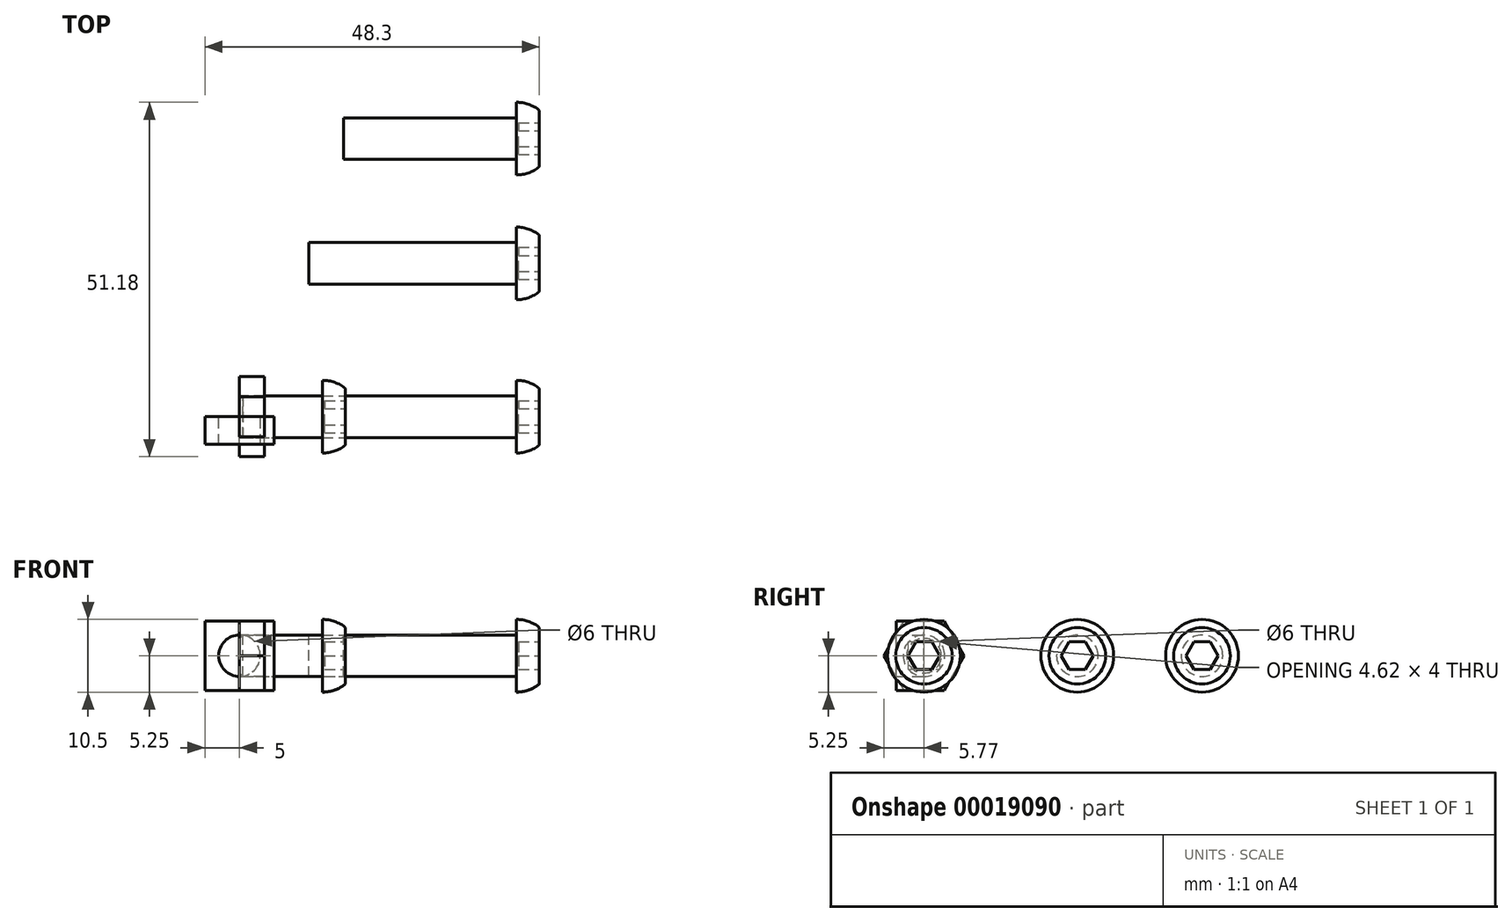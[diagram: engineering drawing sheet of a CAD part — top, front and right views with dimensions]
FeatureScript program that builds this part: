
annotation { "Feature Type Name" : "Feature", "Feature Type Description" : "" }
export const myFeature = defineFeature(function(context is Context, id is Id, definition is map)
    precondition{}
    {
        {
            var Q0;
            Q0=qCreatedBy(makeId("Right.planeOp"),FACE);
            var sketch = newSketch(context, id + "F0", { "sketchPlane" : qUnion([Q0])});
            skCircle(sketch, "E0.cCircle", {"center": v(0, 0) * mm, "radius": 5 * mm, "construction": true});
            skLineSegment(sketch, "E0.0", {"start": v(5.77, 0) * mm, "end": v(2.89, -5) * mm});
            skLineSegment(sketch, "E0.1", {"start": v(2.89, -5) * mm, "end": v(-2.89, -5) * mm});
            skLineSegment(sketch, "E0.2", {"start": v(-2.89, -5) * mm, "end": v(-5.77, 0) * mm});
            skLineSegment(sketch, "E0.3", {"start": v(-5.77, 0) * mm, "end": v(-2.89, 5) * mm});
            skLineSegment(sketch, "E0.4", {"start": v(-2.89, 5) * mm, "end": v(2.89, 5) * mm});
            skLineSegment(sketch, "E0.5", {"start": v(2.89, 5) * mm, "end": v(5.77, 0) * mm});
            skPoint(sketch, "E0.0.midPoint", {"position": v(4.33, -2.5) * mm});
            skLineSegment(sketch, "E1", {"start": v(0, 0) * mm, "end": v(17.46, 0) * mm, "construction": true});
            skCircle(sketch, "E2", {"center": v(0, 0) * mm, "radius": 3 * mm});
            skSolve(sketch);
        }
        {
            var Q0;
            Q0=qCreatedBy(makeId("Top.planeOp"),FACE);
            var sketch = newSketch(context, id + "F1", { "sketchPlane" : qUnion([Q0])});
            skLineSegment(sketch, "E3.top", {"start": v(40, 3) * mm, "end": v(0, 3) * mm});
            skLineSegment(sketch, "E3.bottom", {"start": v(40, 0) * mm, "end": v(0, 0) * mm});
            skLineSegment(sketch, "E3.right", {"start": v(0, 0) * mm, "end": v(0, 3) * mm});
            skPoint(sketch, "E4", {"position": v(41.65, 0) * mm});
            skLineSegment(sketch, "E5.rect.bottom", {"start": v(40, 5.25) * mm, "end": v(43.3, 5.25) * mm, "construction": true});
            skLineSegment(sketch, "E5.rect.top", {"start": v(40, -5.25) * mm, "end": v(43.3, -5.25) * mm, "construction": true});
            skLineSegment(sketch, "E5.rect.left", {"start": v(40, 5.25) * mm, "end": v(40, -5.25) * mm});
            skLineSegment(sketch, "E5.rect.right", {"start": v(43.3, 5.25) * mm, "end": v(43.3, -5.25) * mm});
            skArc(sketch, "E6", {"start": v(43.3, 4.08) * mm, "mid": v(41.75, 4.95) * mm, "end": v(40, 5.25) * mm});
            skArc(sketch, "E7.MirrorCS", {"start": v(43.3, -4.08) * mm, "mid": v(41.75, -4.95) * mm, "end": v(40, -5.25) * mm});
            skLineSegment(sketch, "E8", {"start": v(40, 0) * mm, "end": v(43.3, 0) * mm});
            skLineSegment(sketch, "E9.MirrorCS", {"start": v(0, 0) * mm, "end": v(0, -3) * mm});
            skLineSegment(sketch, "E10.MirrorCS", {"start": v(40, -3) * mm, "end": v(0, -3) * mm});
            skSolve(sketch);
        }
        {
            var Q0;
            Q0=qSketchRegion(id+"F0",true);
            extrude(context, id + "F2", {"entities" : qUnion([Q0]), "depth" : 3.6 * mm});
        }
        {
            var Q0;
            {var subQ2=sQuery(id+"F1.wireOp",EDGE,"E3.top");Q0=makeQuery(id+"F1.imprint","IMPRINT",FACE,{"disambiguationData":[TD([[makeQuery(id+"F1.imprint","IMPRINT",EDGE,{"derivedFrom":subQ2}),1.0]])]});}
            var Q1;
            {var subQ0=sQuery(id+"F1.wireOp",EDGE,"E6");Q1=makeQuery(id+"F1.imprint","IMPRINT",FACE,{"disambiguationData":[TD([[makeQuery(id+"F1.imprint","IMPRINT",EDGE,{"derivedFrom":subQ0}),1.0]])]});}
            var Q2;
            Q2=sQuery(id+"F1.wireOp",EDGE,"E3.bottom");
            revolve(context, id + "F3", {"entities" : qUnion([Q0, Q1]), "axis" : qUnion([Q2]), "revolveType" : RevolveType.FULL});
        }
        {
            var Q0;
            Q0=makeQuery(id+"F3.opRevolve","SWEPT_FACE",FACE,{"disambiguationData":[OSD([sQuery(id+"F1.wireOp",EDGE,"E5.rect.right")])]});
            cPlane(context, id + "F4", {"entities" : qUnion([Q0]), "cplaneType" : CPlaneType.OFFSET, "offset" : 0 * mm, "width" : 150 * mm, "height" : 150 * mm});
        }
        {
            var Q0;
            Q0=qCreatedBy(id+"F4.planeOp",FACE);
            var sketch = newSketch(context, id + "F5", { "sketchPlane" : qUnion([Q0])});
            skCircle(sketch, "E11.cCircle", {"center": v(0, 0) * mm, "radius": 2 * mm, "construction": true});
            skLineSegment(sketch, "E11.0", {"start": v(2.3, 0) * mm, "end": v(1.15, -2) * mm});
            skLineSegment(sketch, "E11.1", {"start": v(1.15, -2) * mm, "end": v(-1.15, -2) * mm});
            skLineSegment(sketch, "E11.2", {"start": v(-1.15, -2) * mm, "end": v(-2.3, 0) * mm});
            skLineSegment(sketch, "E11.3", {"start": v(-2.3, 0) * mm, "end": v(-1.15, 2) * mm});
            skLineSegment(sketch, "E11.4", {"start": v(-1.15, 2) * mm, "end": v(1.15, 2) * mm});
            skLineSegment(sketch, "E11.5", {"start": v(1.15, 2) * mm, "end": v(2.3, 0) * mm});
            skPoint(sketch, "E11.0.midPoint", {"position": v(1.73, -1) * mm});
            skLineSegment(sketch, "E12", {"start": v(0, 0) * mm, "end": v(8.66, 0) * mm, "construction": true});
            skLineSegment(sketch, "E13", {"start": v(0, 0) * mm, "end": v(1.73, -1) * mm, "construction": true});
            skSolve(sketch);
        }
        {
            var Q0;
            Q0=qSketchRegion(id+"F5",true);
            extrude(context, id + "F6", {"entities" : qUnion([Q0]), "operationType" : NewBodyOperationType.REMOVE, "oppositeDirection" : true, "depth" : 3 * mm});
        }
        {
            var Q0;
            Q0=makeQuery(id+"F3.opRevolve","SWEPT_BODY",BODY,{"disambiguationData":[OSD([sQuery(id+"F1.wireOp",EDGE,"E3.top"),sQuery(id+"F1.wireOp",EDGE,"E3.bottom"),sQuery(id+"F1.wireOp",EDGE,"E3.right"),sQuery(id+"F1.wireOp",EDGE,"E5.rect.left"),sQuery(id+"F1.wireOp",EDGE,"E5.rect.right"),sQuery(id+"F1.wireOp",EDGE,"E6"),sQuery(id+"F1.wireOp",EDGE,"E8")])]});
            transform(context, id + "F7", {"entities" : qUnion([Q0]), "transformType" : TransformType.TRANSLATION_3D, "dx" : 0 * mm, "dy" : 22.14 * mm, "dz" : 0 * mm, "makeCopy" : true});
        }
        {
            var Q0;
            Q0=qCreatedBy(makeId("Front.planeOp"),FACE);
            var sketch = newSketch(context, id + "F8", { "sketchPlane" : qUnion([Q0])});
            skLineSegment(sketch, "E14.rect.bottom", {"start": v(5, -5) * mm, "end": v(-5, -5) * mm});
            skLineSegment(sketch, "E14.rect.top", {"start": v(5, 5) * mm, "end": v(-5, 5) * mm});
            skLineSegment(sketch, "E14.rect.left", {"start": v(5, -5) * mm, "end": v(5, 5) * mm});
            skLineSegment(sketch, "E14.rect.right", {"start": v(-5, -5) * mm, "end": v(-5, 5) * mm});
            skPoint(sketch, "E14.rect.middle", {"position": v(0, 0) * mm});
            skCircle(sketch, "E15", {"center": v(0, 0) * mm, "radius": 3 * mm});
            skSolve(sketch);
        }
        {
            var Q0;
            Q0=qSketchRegion(id+"F8",true);
            extrude(context, id + "F9", {"entities" : qUnion([Q0]), "depth" : 4 * mm});
        }
        {
            var Q0;
            Q0=qCreatedBy(makeId("Front.planeOp"),FACE);
            var sketch = newSketch(context, id + "F10", { "sketchPlane" : qUnion([Q0])});
            skLineSegment(sketch, "E16.top", {"start": v(12, 3) * mm, "end": v(0, 3) * mm});
            skLineSegment(sketch, "E16.bottom", {"start": v(12, 0) * mm, "end": v(0, 0) * mm});
            skLineSegment(sketch, "E16.right", {"start": v(0, 0) * mm, "end": v(0, 3) * mm});
            skLineSegment(sketch, "E17.rect.bottom", {"start": v(12, 5.25) * mm, "end": v(15.3, 5.25) * mm, "construction": true});
            skLineSegment(sketch, "E17.rect.top", {"start": v(12, -5.25) * mm, "end": v(15.3, -5.25) * mm, "construction": true});
            skLineSegment(sketch, "E17.rect.left", {"start": v(12, 5.25) * mm, "end": v(12, -5.25) * mm});
            skLineSegment(sketch, "E17.rect.right", {"start": v(15.3, 5.25) * mm, "end": v(15.3, -5.25) * mm});
            skArc(sketch, "E18", {"start": v(15.3, 4.08) * mm, "mid": v(13.75, 4.95) * mm, "end": v(12, 5.25) * mm});
            skArc(sketch, "E19.MirrorCS", {"start": v(15.3, -4.08) * mm, "mid": v(13.75, -4.95) * mm, "end": v(12, -5.25) * mm});
            skLineSegment(sketch, "E20.MirrorCS", {"start": v(0, 0) * mm, "end": v(0, -3) * mm});
            skLineSegment(sketch, "E21.MirrorCS", {"start": v(12, -3) * mm, "end": v(0, -3) * mm});
            skPoint(sketch, "E17.rect.middle", {"position": v(13.65, 0) * mm});
            skLineSegment(sketch, "E22", {"start": v(12, 0) * mm, "end": v(15.3, 0) * mm});
            skSolve(sketch);
        }
        {
            var Q0;
            {var subQ2=sQuery(id+"F10.wireOp",EDGE,"E16.top");Q0=makeQuery(id+"F10.imprint","IMPRINT",FACE,{"disambiguationData":[TD([[makeQuery(id+"F10.imprint","IMPRINT",EDGE,{"derivedFrom":subQ2}),1.0]])]});}
            var Q1;
            {var subQ1=sQuery(id+"F10.wireOp",EDGE,"E18");Q1=makeQuery(id+"F10.imprint","IMPRINT",FACE,{"disambiguationData":[TD([[makeQuery(id+"F10.imprint","IMPRINT",EDGE,{"derivedFrom":subQ1}),1.0]])]});}
            var Q2;
            Q2=sQuery(id+"F10.wireOp",EDGE,"E16.bottom");
            revolve(context, id + "F11", {"entities" : qUnion([Q0, Q1]), "axis" : qUnion([Q2]), "revolveType" : RevolveType.FULL});
        }
        {
            var Q0;
            Q0=makeQuery(id+"F11.opRevolve","SWEPT_FACE",FACE,{"disambiguationData":[OSD([sQuery(id+"F10.wireOp",EDGE,"E17.rect.right")])]});
            cPlane(context, id + "F12", {"entities" : qUnion([Q0]), "cplaneType" : CPlaneType.OFFSET, "offset" : 0 * mm, "width" : 150 * mm, "height" : 150 * mm});
        }
        {
            var Q0;
            Q0=qCreatedBy(id+"F12.planeOp",FACE);
            var sketch = newSketch(context, id + "F13", { "sketchPlane" : qUnion([Q0])});
            skCircle(sketch, "E23.cCircle", {"center": v(0, 0) * mm, "radius": 2 * mm, "construction": true});
            skLineSegment(sketch, "E23.0", {"start": v(2.3, 0) * mm, "end": v(1.15, -2) * mm});
            skLineSegment(sketch, "E23.1", {"start": v(1.15, -2) * mm, "end": v(-1.15, -2) * mm});
            skLineSegment(sketch, "E23.2", {"start": v(-1.15, -2) * mm, "end": v(-2.3, 0) * mm});
            skLineSegment(sketch, "E23.3", {"start": v(-2.3, 0) * mm, "end": v(-1.15, 2) * mm});
            skLineSegment(sketch, "E23.4", {"start": v(-1.15, 2) * mm, "end": v(1.15, 2) * mm});
            skLineSegment(sketch, "E23.5", {"start": v(1.15, 2) * mm, "end": v(2.3, 0) * mm});
            skPoint(sketch, "E23.0.midPoint", {"position": v(1.73, -1) * mm});
            skLineSegment(sketch, "E24", {"start": v(0, 0) * mm, "end": v(5.46, 0) * mm, "construction": true});
            skLineSegment(sketch, "E25", {"start": v(0, 0) * mm, "end": v(1.73, -1) * mm, "construction": true});
            skSolve(sketch);
        }
        {
            var Q0;
            Q0=qSketchRegion(id+"F13",true);
            extrude(context, id + "F14", {"entities" : qUnion([Q0]), "operationType" : NewBodyOperationType.REMOVE, "oppositeDirection" : true, "depth" : 3 * mm});
        }
        {
            var Q0;
            Q0=makeQuery(id+"F7.opPattern","COPY",FACE,{"derivedFrom":makeQuery(id+"F3.opRevolve","SWEPT_FACE",FACE,{"disambiguationData":[OSD([sQuery(id+"F1.wireOp",EDGE,"E3.right")])]}),"instanceName":"1"});
            extrude(context, id + "F15", {"entities" : qUnion([Q0]), "operationType" : NewBodyOperationType.REMOVE, "oppositeDirection" : true, "depth" : 10 * mm});
        }
        {
            var Q0;
            Q0=makeQuery(id+"F15.boolean.opBoolean","COPY",FACE,{"derivedFrom":makeQuery(id+"F15.opExtrude","CAP_FACE",FACE,{"disambiguationData":[OSD([sQuery(id+"F1.wireOp",EDGE,"E3.right")])],"isStart":false})});
            var sketch = newSketch(context, id + "F16", { "sketchPlane" : qUnion([Q0])});
            skPoint(sketch, "E26", {"position": v(-22.14, 0) * mm});
            skSolve(sketch);
        }
        {
            var Q0;
            Q0=makeQuery(id+"F7.opPattern","COPY",FACE,{"derivedFrom":makeQuery(id+"F3.opRevolve","SWEPT_FACE",FACE,{"disambiguationData":[OSD([sQuery(id+"F1.wireOp",EDGE,"E5.rect.left")])]}),"instanceName":"1"});
            var sketch = newSketch(context, id + "F17", { "sketchPlane" : qUnion([Q0])});
            skPoint(sketch, "E27", {"position": v(-22.14, 0) * mm});
            skSolve(sketch);
        }
        {
            var Q0;
            Q0=qCreatedBy(makeId("Top.planeOp"),FACE);
            var Q1;
            Q1=sQuery(id+"F16.wireOp",VERTEX,"E26");
            cPlane(context, id + "F18", {"entities" : qUnion([Q0, Q1]), "cplaneType" : CPlaneType.PLANE_POINT, "offset" : 150 * mm, "width" : 150 * mm, "height" : 150 * mm});
        }
        {
            var Q0;
            Q0=makeQuery(id+"F7.opPattern","COPY",BODY,{"derivedFrom":makeQuery(id+"F3.opRevolve","SWEPT_BODY",BODY,{"disambiguationData":[OSD([sQuery(id+"F1.wireOp",EDGE,"E3.top"),sQuery(id+"F1.wireOp",EDGE,"E3.bottom"),sQuery(id+"F1.wireOp",EDGE,"E3.right"),sQuery(id+"F1.wireOp",EDGE,"E5.rect.left"),sQuery(id+"F1.wireOp",EDGE,"E5.rect.right"),sQuery(id+"F1.wireOp",EDGE,"E6"),sQuery(id+"F1.wireOp",EDGE,"E8")])]}),"instanceName":"1"});
            transform(context, id + "F19", {"entities" : qUnion([Q0]), "transformType" : TransformType.TRANSLATION_3D, "dx" : 0 * mm, "dy" : 18.02 * mm, "dz" : 0 * mm, "makeCopy" : true});
        }
        {
            var Q0;
            Q0=makeQuery(id+"F19.opPattern","COPY",FACE,{"derivedFrom":makeQuery(id+"F15.boolean.opBoolean","COPY",FACE,{"derivedFrom":makeQuery(id+"F15.opExtrude","CAP_FACE",FACE,{"disambiguationData":[OSD([sQuery(id+"F1.wireOp",EDGE,"E3.right")])],"isStart":false})}),"instanceName":"1"});
            extrude(context, id + "F20", {"entities" : qUnion([Q0]), "operationType" : NewBodyOperationType.REMOVE, "oppositeDirection" : true, "depth" : 5 * mm});
        }
        {
            var Q0;
            Q0=makeQuery(id+"F3.opRevolve","SWEPT_EDGE",EDGE,{"disambiguationData":[OSD([sQuery(id+"F1.wireOp",EDGE,"E3.top"),sQuery(id+"F1.wireOp",EDGE,"E3.right")])]});
            var Q1;
            Q1=makeQuery(id+"F15.boolean.opBoolean","COPY",EDGE,{"derivedFrom":makeQuery(id+"F15.opExtrude","CAP_EDGE",EDGE,{"disambiguationData":[OSD([sQuery(id+"F1.wireOp",EDGE,"E3.top"),sQuery(id+"F1.wireOp",EDGE,"E3.right")])],"isStart":false})});
            var Q2;
            Q2=makeQuery(id+"F20.boolean.opBoolean","COPY",EDGE,{"derivedFrom":makeQuery(id+"F20.opExtrude","CAP_EDGE",EDGE,{"disambiguationData":[OSD([sQuery(id+"F1.wireOp",EDGE,"E3.top"),sQuery(id+"F1.wireOp",EDGE,"E3.right")])],"isStart":false})});
            chamfer(context, id + "F21", {"entities" : qUnion([Q0, Q1, Q2]), "width" : 0.5 * mm, "tangentPropagation" : true});
        }
    });
